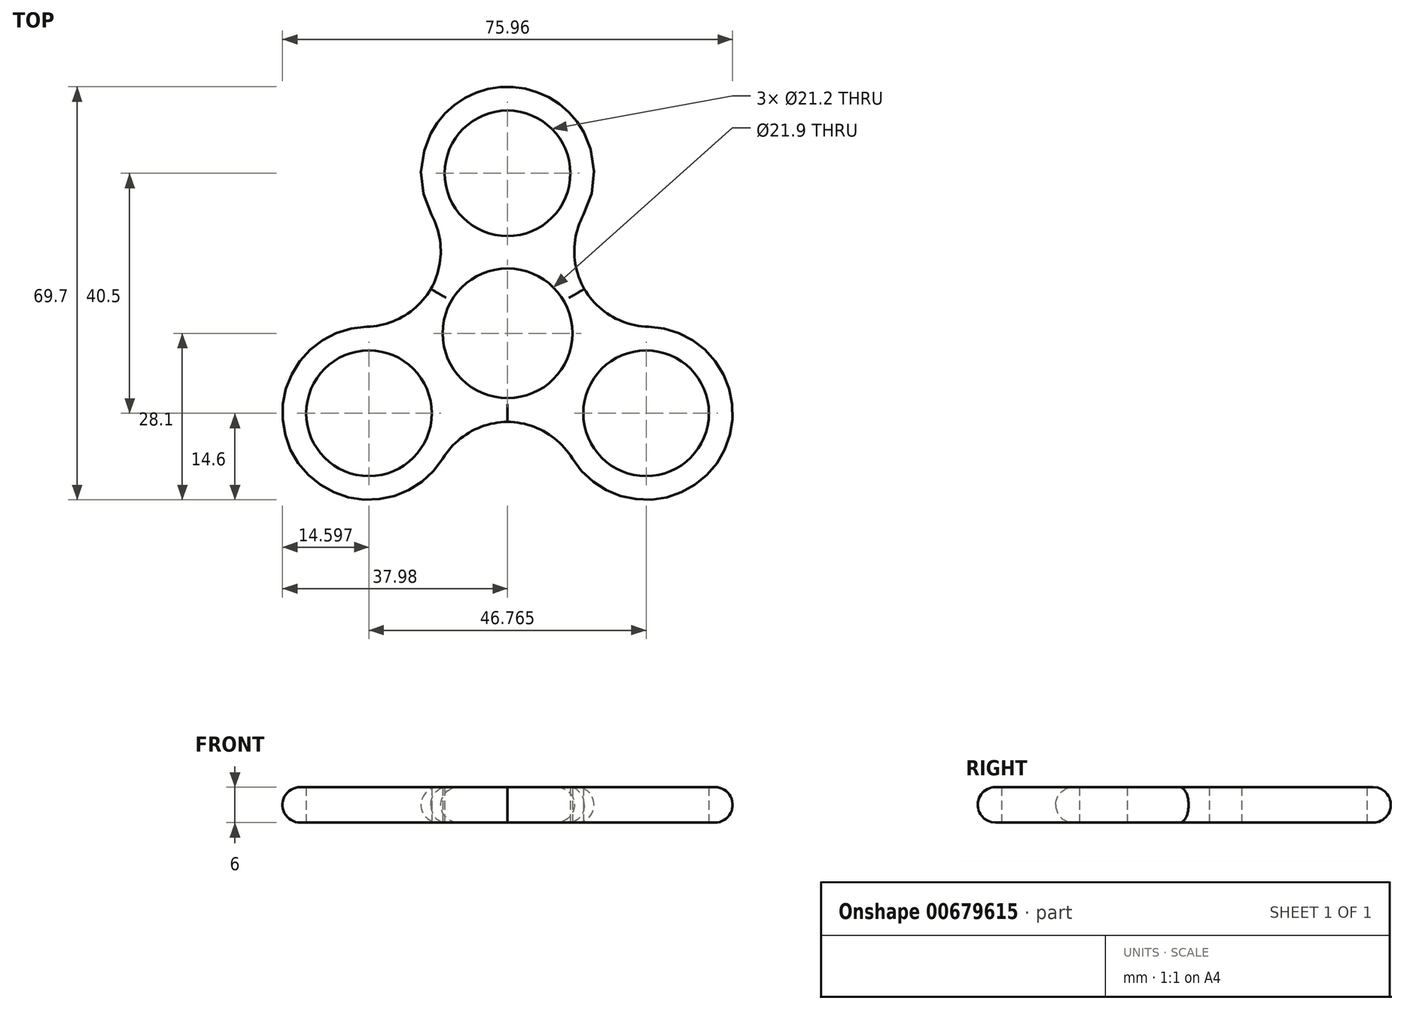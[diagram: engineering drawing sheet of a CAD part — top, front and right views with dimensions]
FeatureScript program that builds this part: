
annotation { "Feature Type Name" : "Feature", "Feature Type Description" : "" }
export const myFeature = defineFeature(function(context is Context, id is Id, definition is map)
    precondition{}
    {
        {
            var Q0;
            Q0=qCreatedBy(makeId("Top.planeOp"),FACE);
            var sketch = newSketch(context, id + "F0", { "sketchPlane" : qUnion([Q0])});
            skCircle(sketch, "E0", {"center": v(0, 0) * mm, "radius": 10.95 * mm});
            skCircle(sketch, "E1.cCircle", {"center": v(0, 0) * mm, "radius": 13.5 * mm, "construction": true});
            skLineSegment(sketch, "E1.0", {"start": v(-23.38, -13.5) * mm, "end": v(0, 27) * mm, "construction": true});
            skLineSegment(sketch, "E1.1", {"start": v(0, 27) * mm, "end": v(23.38, -13.5) * mm, "construction": true});
            skLineSegment(sketch, "E1.2", {"start": v(23.38, -13.5) * mm, "end": v(-23.38, -13.5) * mm, "construction": true});
            skPoint(sketch, "E1.0.midPoint", {"position": v(-11.7, 6.75) * mm});
            skCircle(sketch, "E2", {"center": v(0, 27) * mm, "radius": 10.6 * mm});
            skCircle(sketch, "E3", {"center": v(23.38, -13.5) * mm, "radius": 10.6 * mm});
            skCircle(sketch, "E4", {"center": v(-23.38, -13.5) * mm, "radius": 10.6 * mm});
            skCircle(sketch, "E5.0", {"center": v(-23.38, -13.5) * mm, "radius": 14.6 * mm});
            skCircle(sketch, "E6.0", {"center": v(23.38, -13.5) * mm, "radius": 14.6 * mm});
            skCircle(sketch, "E7.0", {"center": v(0, 27) * mm, "radius": 14.6 * mm});
            skCircle(sketch, "E8.0", {"center": v(0, 0) * mm, "radius": 14.95 * mm});
            skSolve(sketch);
        }
        {
            var Q0;
            Q0=qSketchRegion(id+"F0",true);
            extrude(context, id + "F1", {"entities" : qUnion([Q0]), "depth" : 6 * mm, "offsetDistance" : 25 * mm});
        }
        {
            var Q0;
            {var subQ0=sQuery(id+"F0.wireOp",EDGE,"E8.0");var subQ1=sQuery(id+"F0.wireOp",EDGE,"E5.0");Q0=makeQuery(id+"F1.opExtrude","SWEPT_EDGE",EDGE,{"disambiguationData":[OSD([subQ1,subQ0]),TDD([makeQuery(id+"F0.imprint","INTERSECT",VERTEX,{"disambiguationData":[OD(1.0)],"derivedFrom":[subQ1,subQ0]})])]});}
            var Q1;
            {var subQ0=sQuery(id+"F0.wireOp",EDGE,"E8.0");var subQ1=sQuery(id+"F0.wireOp",EDGE,"E6.0");Q1=makeQuery(id+"F1.opExtrude","SWEPT_EDGE",EDGE,{"disambiguationData":[OSD([subQ1,subQ0]),TDD([makeQuery(id+"F0.imprint","INTERSECT",VERTEX,{"disambiguationData":[OD(0.0)],"derivedFrom":[subQ1,subQ0]})])]});}
            var Q2;
            {var subQ0=sQuery(id+"F0.wireOp",EDGE,"E8.0");var subQ1=sQuery(id+"F0.wireOp",EDGE,"E7.0");Q2=makeQuery(id+"F1.opExtrude","SWEPT_EDGE",EDGE,{"disambiguationData":[OSD([subQ1,subQ0]),TDD([makeQuery(id+"F0.imprint","INTERSECT",VERTEX,{"disambiguationData":[OD(1.0)],"derivedFrom":[subQ1,subQ0]})])]});}
            var Q3;
            {var subQ0=sQuery(id+"F0.wireOp",EDGE,"E8.0");var subQ1=sQuery(id+"F0.wireOp",EDGE,"E6.0");Q3=makeQuery(id+"F1.opExtrude","SWEPT_EDGE",EDGE,{"disambiguationData":[OSD([subQ1,subQ0]),TDD([makeQuery(id+"F0.imprint","INTERSECT",VERTEX,{"disambiguationData":[OD(1.0)],"derivedFrom":[subQ1,subQ0]})])]});}
            var Q4;
            {var subQ0=sQuery(id+"F0.wireOp",EDGE,"E8.0");var subQ1=sQuery(id+"F0.wireOp",EDGE,"E7.0");Q4=makeQuery(id+"F1.opExtrude","SWEPT_EDGE",EDGE,{"disambiguationData":[OSD([subQ1,subQ0]),TDD([makeQuery(id+"F0.imprint","INTERSECT",VERTEX,{"disambiguationData":[OD(0.0)],"derivedFrom":[subQ1,subQ0]})])]});}
            var Q5;
            {var subQ0=sQuery(id+"F0.wireOp",EDGE,"E8.0");var subQ1=sQuery(id+"F0.wireOp",EDGE,"E5.0");Q5=makeQuery(id+"F1.opExtrude","SWEPT_EDGE",EDGE,{"disambiguationData":[OSD([subQ1,subQ0]),TDD([makeQuery(id+"F0.imprint","INTERSECT",VERTEX,{"disambiguationData":[OD(0.0)],"derivedFrom":[subQ1,subQ0]})])]});}
            fillet(context, id + "F2", {"entities" : qUnion([Q0, Q1, Q2, Q3, Q4, Q5]), "radius" : 13 * mm, "tangentPropagation" : true, "allowEdgeOverflow" : false});
        }
        {
            var Q0;
            Q0=makeQuery(id+"F1.opExtrude","CAP_EDGE",EDGE,{"disambiguationData":[OSD([sQuery(id+"F0.wireOp",EDGE,"E7.0")])],"isStart":false});
            var Q1;
            Q1=makeQuery(id+"F1.opExtrude","CAP_EDGE",EDGE,{"disambiguationData":[OSD([sQuery(id+"F0.wireOp",EDGE,"E7.0")])],"isStart":true});
            var Q2;
            Q2=makeQuery(id+"F1.opExtrude","CAP_EDGE",EDGE,{"disambiguationData":[OSD([sQuery(id+"F0.wireOp",EDGE,"E5.0")])],"isStart":false});
            var Q3;
            Q3=makeQuery(id+"F1.opExtrude","CAP_EDGE",EDGE,{"disambiguationData":[OSD([sQuery(id+"F0.wireOp",EDGE,"E5.0")])],"isStart":true});
            var Q4;
            Q4=makeQuery(id+"F1.opExtrude","CAP_EDGE",EDGE,{"disambiguationData":[OSD([sQuery(id+"F0.wireOp",EDGE,"E6.0")])],"isStart":false});
            var Q5;
            Q5=makeQuery(id+"F1.opExtrude","CAP_EDGE",EDGE,{"disambiguationData":[OSD([sQuery(id+"F0.wireOp",EDGE,"E6.0")])],"isStart":true});
            fillet(context, id + "F3", {"entities" : qUnion([Q0, Q1, Q2, Q3, Q4, Q5]), "radius" : 3 * mm, "tangentPropagation" : true, "allowEdgeOverflow" : false});
        }
    });
